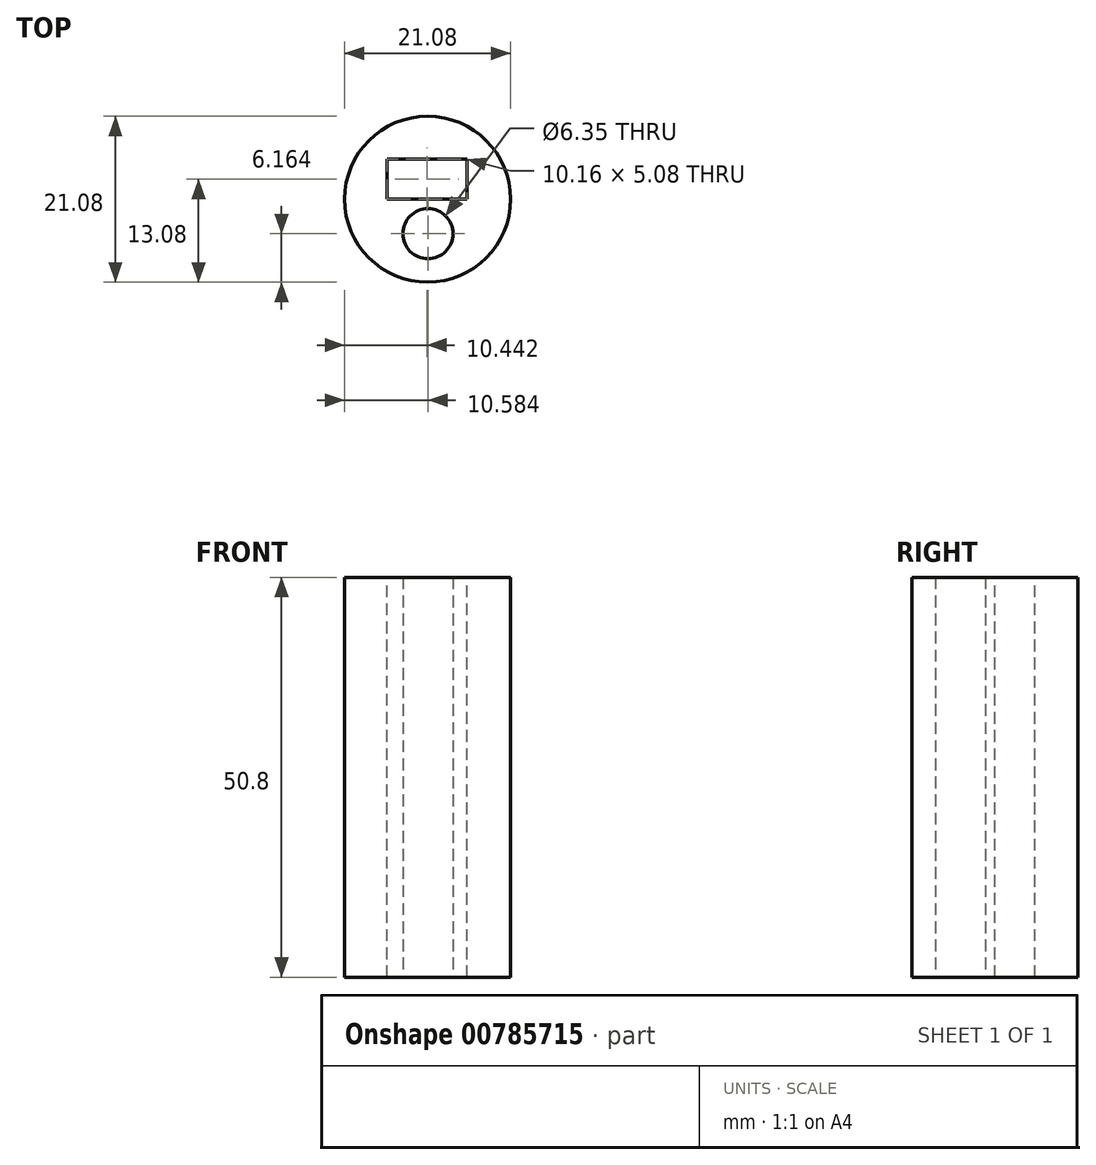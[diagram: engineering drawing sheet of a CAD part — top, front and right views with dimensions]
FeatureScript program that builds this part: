
annotation { "Feature Type Name" : "Feature", "Feature Type Description" : "" }
export const myFeature = defineFeature(function(context is Context, id is Id, definition is map)
    precondition{}
    {
        {
            var Q0;
            Q0=qCreatedBy(makeId("Top.planeOp"),FACE);
            var sketch = newSketch(context, id + "F0", { "sketchPlane" : qUnion([Q0])});
            skCircle(sketch, "E0", {"center": v(0, 0) * mm, "radius": 10.54 * mm});
            skSolve(sketch);
        }
        {
            var Q0;
            Q0 = qSketchRegion(id + "F0", true);
            extrude(context, id + "F1", {"entities" : qUnion([Q0]), "depth" : 25.4 * mm, "offsetDistance" : 25.4 * mm, "hasSecondDirection" : true, "secondDirectionOppositeDirection" : true, "secondDirectionDepth" : 25.4 * mm});
        }
        {
            var Q0;
            Q0=qCreatedBy(makeId("Top.planeOp"),FACE);
            var sketch = newSketch(context, id + "F2", { "sketchPlane" : qUnion([Q0])});
            skLineSegment(sketch, "E1.bottom", {"start": v(-5.18, 0) * mm, "end": v(4.98, 0) * mm});
            skLineSegment(sketch, "E1.top", {"start": v(-5.18, 5.08) * mm, "end": v(4.98, 5.08) * mm});
            skLineSegment(sketch, "E1.left", {"start": v(-5.18, 0) * mm, "end": v(-5.18, 5.08) * mm});
            skLineSegment(sketch, "E1.right", {"start": v(4.98, 0) * mm, "end": v(4.98, 5.08) * mm});
            skSolve(sketch);
        }
        {
            var Q0;
            Q0 = qSketchRegion(id + "F2", true);
            extrude(context, id + "F3", {"entities" : qUnion([Q0]), "operationType" : NewBodyOperationType.REMOVE, "oppositeDirection" : true, "depth" : 25.4 * mm, "offsetDistance" : 25.4 * mm, "hasSecondDirection" : true, "secondDirectionOppositeDirection" : false, "secondDirectionDepth" : 25.4 * mm});
        }
        {
            var Q0;
            Q0=qCreatedBy(makeId("Top.planeOp"),FACE);
            var sketch = newSketch(context, id + "F4", { "sketchPlane" : qUnion([Q0])});
            skCircle(sketch, "E2", {"center": v(0.04, -4.38) * mm, "radius": 3.18 * mm});
            skPoint(sketch, "E2.first.point", {"position": v(0, -1.2) * mm});
            skPoint(sketch, "E2.second.point", {"position": v(0, -7.55) * mm});
            skPoint(sketch, "E2.third.point", {"position": v(-2.97, -5.36) * mm});
            skSolve(sketch);
        }
        {
            var Q0;
            Q0 = qSketchRegion(id + "F4", true);
            extrude(context, id + "F5", {"entities" : qUnion([Q0]), "operationType" : NewBodyOperationType.REMOVE, "depth" : 25.4 * mm, "offsetDistance" : 25.4 * mm, "hasSecondDirection" : true, "secondDirectionOppositeDirection" : true, "secondDirectionDepth" : 25.4 * mm});
        }
    });
